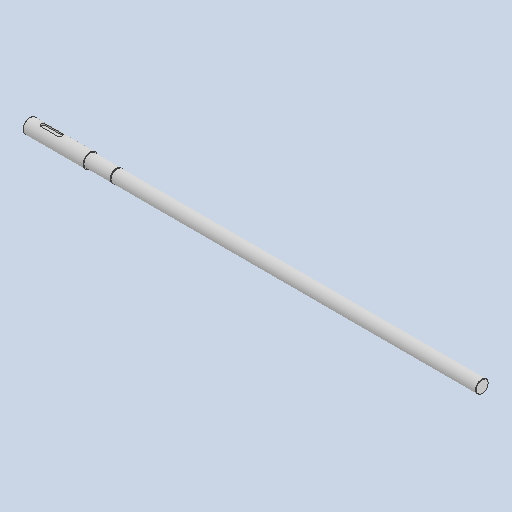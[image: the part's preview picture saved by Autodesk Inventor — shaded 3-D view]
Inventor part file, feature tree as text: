
AUTODESK INVENTOR PART (.ipt)
format: ipt  version: 2025 (Build 290162010, 162A)  size: 136,704 bytes
history: native  units: mm
features: other x8, chamfer x2, revolve x1
ambient origin geometry x6: Origin, XZ Plane, XY Plane, X Axis, Y Axis, Z Axis
bodies: Solid1 (feature_tree)
feature tree (11):
  other  "{BB8FE430-83BF-418D-8DF9-9B323D3DB9B9}"
  revolve  "Revolution1"  [1 undecoded]
  chamfer  "Chamfer1"  Distance=19.0mm
  other  "Keyway1"
  chamfer  "Chamfer2"  Distance=17.0mm
  other  "Retaining Ring Groove1"
  other  "Start Plane"
  other  "Origin point"
  other  "Main Sketch"
  other  "iFeature11:1"
  other  "iFeature27:1"
note: 1 required parameter value undecoded (feature->parameter linkage not recoverable at this tier; creation-order binding heuristic only, values carry confidence <= 0.55)
